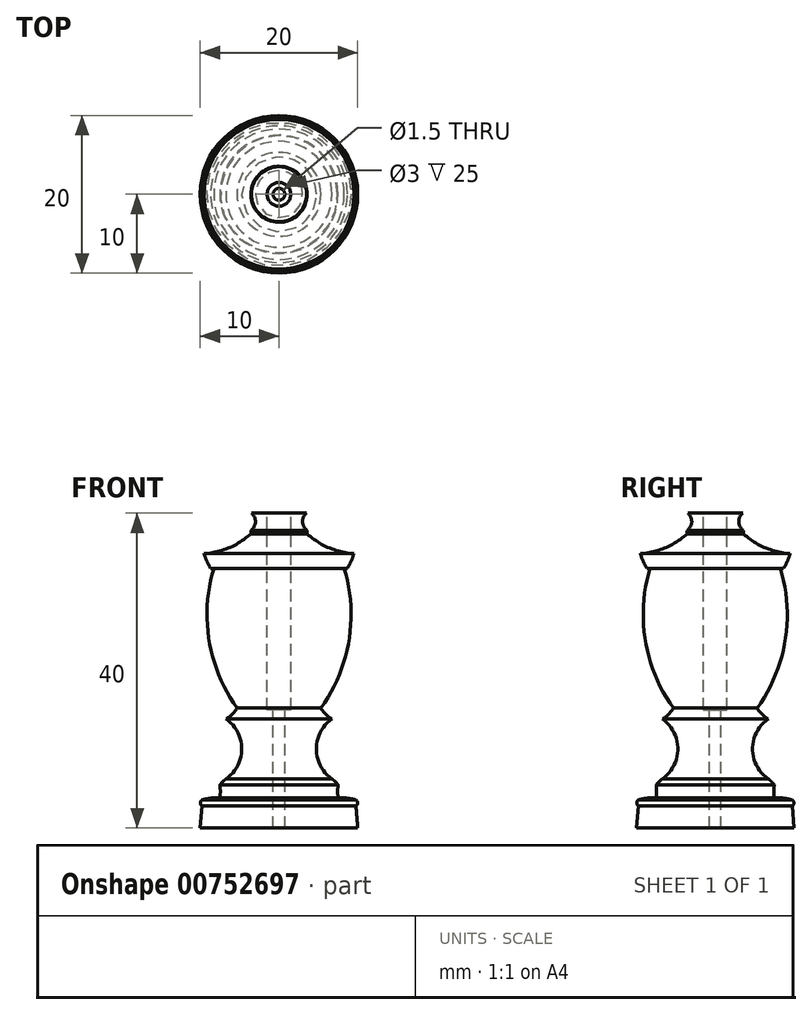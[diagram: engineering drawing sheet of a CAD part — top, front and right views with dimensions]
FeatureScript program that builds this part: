
annotation { "Feature Type Name" : "Feature", "Feature Type Description" : "" }
export const myFeature = defineFeature(function(context is Context, id is Id, definition is map)
    precondition{}
    {
        {
            var Q0;
            Q0=qCreatedBy(makeId("Front.planeOp"),FACE);
            var sketch = newSketch(context, id + "F0", { "sketchPlane" : qUnion([Q0])});
            skLineSegment(sketch, "E0", {"start": v(0, 0) * mm, "end": v(10, 0) * mm});
            skLineSegment(sketch, "E1", {"start": v(10, 0) * mm, "end": v(10, 40) * mm});
            skLineSegment(sketch, "E2", {"start": v(10, 40) * mm, "end": v(0, 40) * mm});
            skLineSegment(sketch, "E3", {"start": v(0, 40) * mm, "end": v(0, 0) * mm});
            skLineSegment(sketch, "E4", {"start": v(10, 0) * mm, "end": v(9.78, 2.78) * mm});
            skArc(sketch, "E5", {"start": v(9.78, 2.78) * mm, "mid": v(9.98, 3.17) * mm, "end": v(9.78, 3.56) * mm});
            skArc(sketch, "E6", {"start": v(9.78, 3.56) * mm, "mid": v(8.66, 3.79) * mm, "end": v(7.5, 3.83) * mm});
            skArc(sketch, "E7", {"start": v(7.5, 5.47) * mm, "mid": v(7.45, 4.65) * mm, "end": v(7.5, 3.83) * mm});
            skArc(sketch, "E8", {"start": v(7.5, 5.47) * mm, "mid": v(7.14, 5.89) * mm, "end": v(6.73, 6.25) * mm});
            skArc(sketch, "E9", {"start": v(6.73, 13.84) * mm, "mid": v(4.74, 10.04) * mm, "end": v(6.73, 6.25) * mm});
            skArc(sketch, "E10", {"start": v(5.33, 15.22) * mm, "mid": v(5.94, 14.44) * mm, "end": v(6.73, 13.84) * mm});
            skArc(sketch, "E11", {"start": v(5.33, 15.22) * mm, "mid": v(8.87, 23.76) * mm, "end": v(8.28, 32.99) * mm});
            skArc(sketch, "E12", {"start": v(3.56, 37.38) * mm, "mid": v(6.32, 35.6) * mm, "end": v(9.51, 34.84) * mm});
            skArc(sketch, "E13", {"start": v(3.56, 37.38) * mm, "mid": v(3.57, 37.59) * mm, "end": v(3.56, 37.8) * mm});
            skArc(sketch, "E14", {"start": v(3.5, 40) * mm, "mid": v(2.99, 38.89) * mm, "end": v(3.56, 37.8) * mm});
            skLineSegment(sketch, "E15", {"start": v(8.28, 32.99) * mm, "end": v(8.68, 32.99) * mm});
            skArc(sketch, "E16", {"start": v(8.68, 32.99) * mm, "mid": v(9.16, 33.89) * mm, "end": v(9.51, 34.84) * mm});
            skSolve(sketch);
        }
        {
            var Q0;
            Q0=makeQuery(id+"F0.imprint","IMPRINT",FACE,{"disambiguationData":[TD([[makeQuery(id+"F0.imprint","IMPRINT",EDGE,{"derivedFrom":sQuery(id+"F0.wireOp",EDGE,"E0")}),1.0]])]});
            var Q1;
            Q1=sQuery(id+"F0.wireOp",EDGE,"E3");
            revolve(context, id + "F1", {"surfaceOperationType" : NewSurfaceOperationType.NEW, "entities" : qUnion([Q0]), "axis" : qUnion([Q1]), "revolveType" : RevolveType.FULL});
        }
        {
            var Q0;
            Q0=makeQuery(id+"F1.opRevolve","SWEPT_FACE",FACE,{"disambiguationData":[OSD([sQuery(id+"F0.wireOp",EDGE,"E2")])]});
            var sketch = newSketch(context, id + "F2", { "sketchPlane" : qUnion([Q0])});
            skCircle(sketch, "E17", {"center": v(0, 0) * mm, "radius": 1.5 * mm});
            skCircle(sketch, "E18", {"center": v(0, 0) * mm, "radius": 0.75 * mm});
            skSolve(sketch);
        }
        {
            var Q0;
            Q0=makeQuery(id+"F2.imprint","IMPRINT",FACE,{"disambiguationData":[TD([[makeQuery(id+"F2.imprint","IMPRINT",EDGE,{"derivedFrom":sQuery(id+"F2.wireOp",EDGE,"E18")}),1.0]])]});
            var Q1;
            Q1=makeQuery(id+"F1.opRevolve","SWEPT_BODY",BODY,{"disambiguationData":[OSD([sQuery(id+"F0.wireOp",EDGE,"E0"),sQuery(id+"F0.wireOp",EDGE,"E2"),sQuery(id+"F0.wireOp",EDGE,"E3"),sQuery(id+"F0.wireOp",EDGE,"E4"),sQuery(id+"F0.wireOp",EDGE,"E5"),sQuery(id+"F0.wireOp",EDGE,"E6"),sQuery(id+"F0.wireOp",EDGE,"E7"),sQuery(id+"F0.wireOp",EDGE,"E8"),sQuery(id+"F0.wireOp",EDGE,"E9"),sQuery(id+"F0.wireOp",EDGE,"E10"),sQuery(id+"F0.wireOp",EDGE,"E11"),sQuery(id+"F0.wireOp",EDGE,"E12"),sQuery(id+"F0.wireOp",EDGE,"E13"),sQuery(id+"F0.wireOp",EDGE,"E14"),sQuery(id+"F0.wireOp",EDGE,"E15"),sQuery(id+"F0.wireOp",EDGE,"E16")])]});
            extrude(context, id + "F3", {"entities" : qUnion([Q0]), "operationType" : NewBodyOperationType.REMOVE, "endBound" : BoundingType.THROUGH_ALL, "oppositeDirection" : true, "depth" : 25 * mm, "endBoundEntityBody" : qUnion([Q1]), "offsetDistance" : 25 * mm});
        }
        {
            var Q0;
            Q0=makeQuery(id+"F2.imprint","IMPRINT",FACE,{"disambiguationData":[TD([[makeQuery(id+"F2.imprint","IMPRINT",EDGE,{"derivedFrom":sQuery(id+"F2.wireOp",EDGE,"E17")}),1.0]])]});
            extrude(context, id + "F4", {"entities" : qUnion([Q0]), "operationType" : NewBodyOperationType.REMOVE, "oppositeDirection" : true, "depth" : 25 * mm, "offsetDistance" : 25 * mm});
        }
    });
